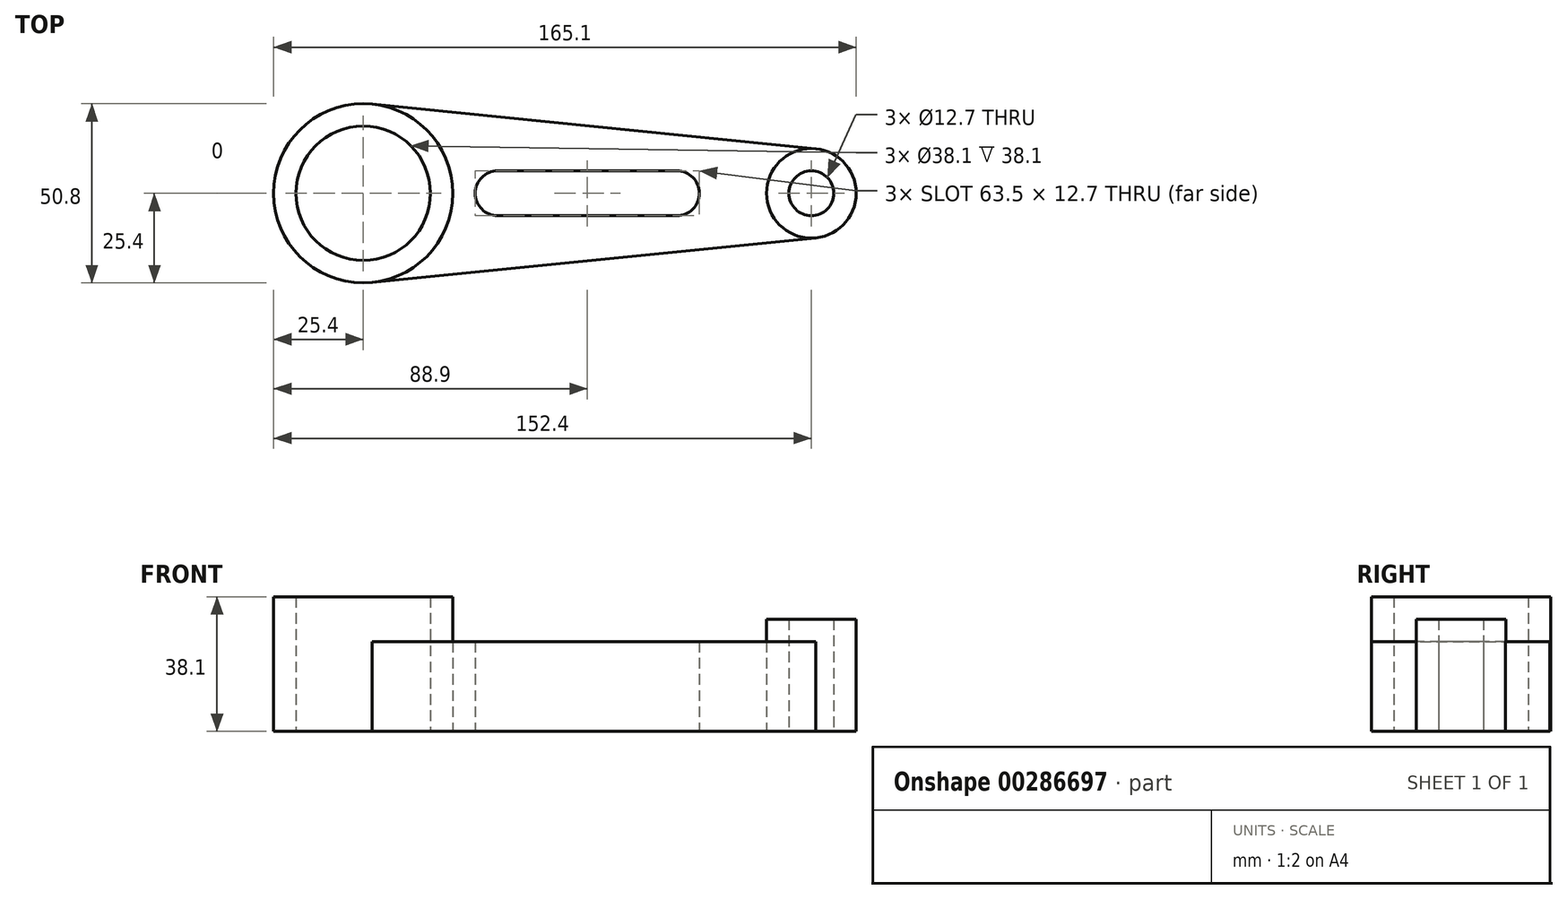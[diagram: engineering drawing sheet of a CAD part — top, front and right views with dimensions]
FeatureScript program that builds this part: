
annotation { "Feature Type Name" : "Feature", "Feature Type Description" : "" }
export const myFeature = defineFeature(function(context is Context, id is Id, definition is map)
    precondition{}
    {
        {
            var Q0;
            Q0=qCreatedBy(makeId("Top.planeOp"),FACE);
            var sketch = newSketch(context, id + "F0", { "sketchPlane" : qUnion([Q0])});
            skCircle(sketch, "E0", {"center": v(-38.1, 0) * mm, "radius": 19.05 * mm});
            skCircle(sketch, "E1", {"center": v(-38.1, 0) * mm, "radius": 25.4 * mm});
            skCircle(sketch, "E2", {"center": v(88.9, 0) * mm, "radius": 6.35 * mm});
            skCircle(sketch, "E3", {"center": v(88.9, 0) * mm, "radius": 12.7 * mm});
            skLineSegment(sketch, "E4", {"start": v(-35.56, 25.27) * mm, "end": v(90.17, 12.64) * mm});
            skLineSegment(sketch, "E5", {"start": v(-35.56, -25.27) * mm, "end": v(90.17, -12.64) * mm});
            skCircle(sketch, "E6", {"center": v(0, 0) * mm, "radius": 6.35 * mm});
            skCircle(sketch, "E7", {"center": v(50.8, 0) * mm, "radius": 6.35 * mm});
            skLineSegment(sketch, "E8", {"start": v(0, 6.35) * mm, "end": v(50.8, 6.35) * mm});
            skLineSegment(sketch, "E9", {"start": v(50.8, -6.35) * mm, "end": v(0, -6.35) * mm});
            skSolve(sketch);
        }
        {
            var Q0;
            Q0=makeQuery(id+"F0.imprint","IMPRINT",FACE,{"disambiguationData":[TD([[makeQuery(id+"F0.imprint","IMPRINT",EDGE,{"derivedFrom":sQuery(id+"F0.wireOp",EDGE,"E2")}),-1.0]])]});
            extrude(context, id + "F1", {"entities" : qUnion([Q0]), "depth" : 31.75 * mm});
        }
        {
            var Q0;
            Q0=makeQuery(id+"F0.imprint","IMPRINT",FACE,{"disambiguationData":[TD([[makeQuery(id+"F0.imprint","IMPRINT",EDGE,{"derivedFrom":sQuery(id+"F0.wireOp",EDGE,"E0")}),-1.0]])]});
            extrude(context, id + "F2", {"entities" : qUnion([Q0]), "depth" : 38.1 * mm});
        }
        {
            var Q0;
            {var subQ0=sQuery(id+"F0.wireOp",EDGE,"E4");Q0=makeQuery(id+"F0.imprint","IMPRINT",FACE,{"disambiguationData":[TD([[makeQuery(id+"F0.imprint","IMPRINT",EDGE,{"derivedFrom":subQ0}),-1.0]])]});}
            extrude(context, id + "F3", {"entities" : qUnion([Q0]), "depth" : 25.4 * mm});
        }
    });
